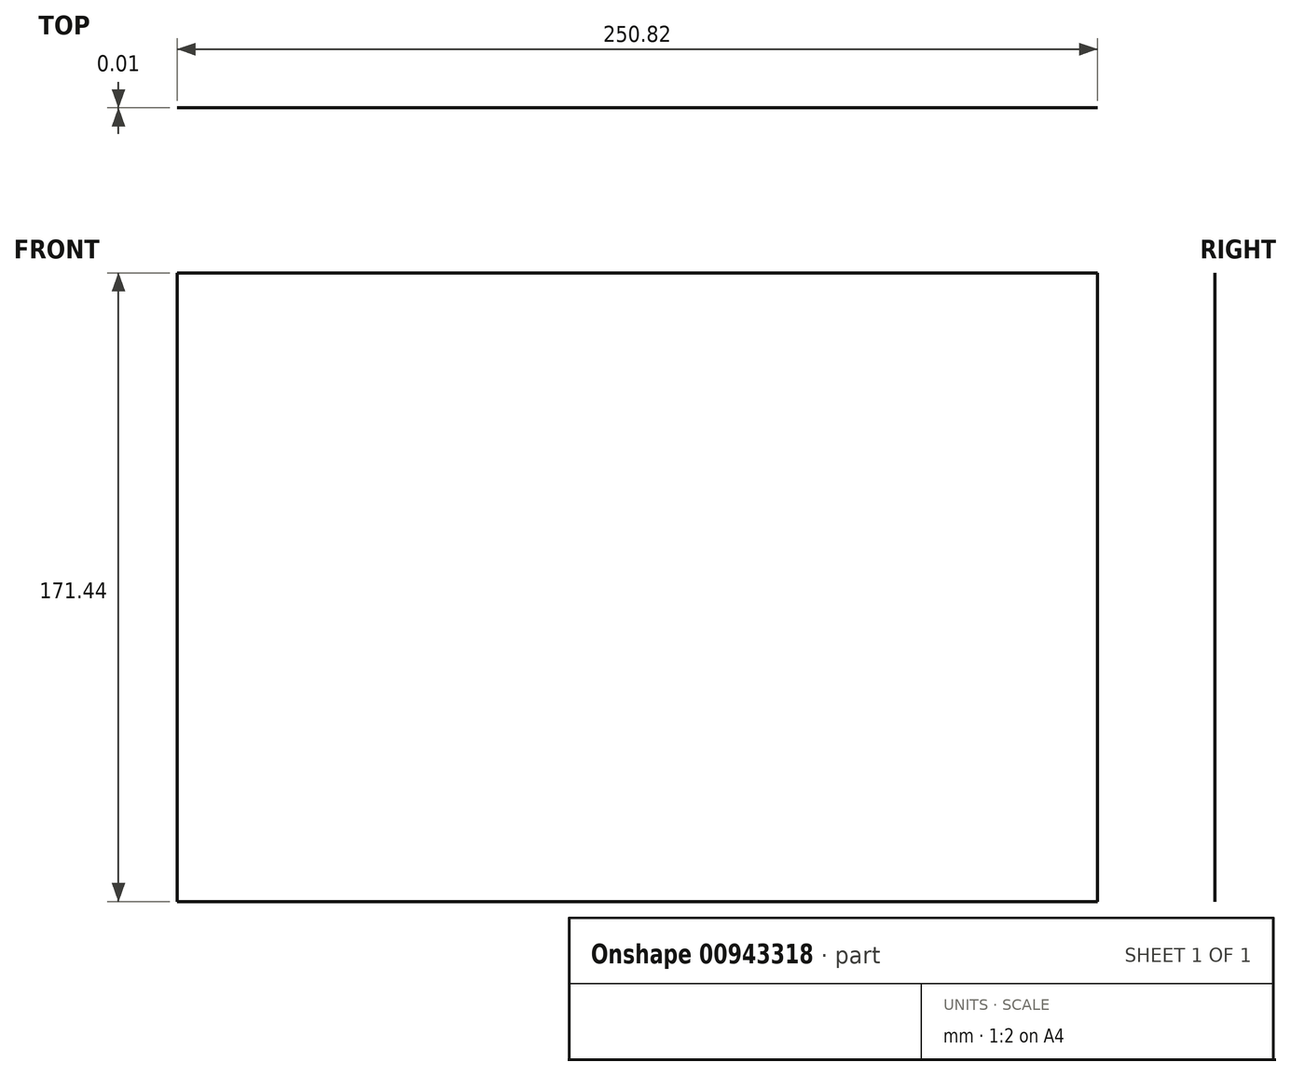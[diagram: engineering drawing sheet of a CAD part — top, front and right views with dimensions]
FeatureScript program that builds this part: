
annotation { "Feature Type Name" : "Feature", "Feature Type Description" : "" }
export const myFeature = defineFeature(function(context is Context, id is Id, definition is map)
    precondition{}
    {
        {
            var Q0;
            Q0=qCreatedBy(makeId("Front.planeOp"),FACE);
            var sketch = newSketch(context, id + "F0", { "sketchPlane" : qUnion([Q0])});
            skLineSegment(sketch, "E0.bottom", {"start": v(125.41, 85.73) * mm, "end": v(-125.41, 85.73) * mm});
            skLineSegment(sketch, "E0.top", {"start": v(125.41, -85.73) * mm, "end": v(-125.41, -85.73) * mm});
            skLineSegment(sketch, "E0.left", {"start": v(125.41, 85.73) * mm, "end": v(125.41, -85.73) * mm});
            skLineSegment(sketch, "E0.right", {"start": v(-125.41, 85.73) * mm, "end": v(-125.41, -85.73) * mm});
            skPoint(sketch, "E0.middle", {"position": v(0, 0) * mm});
            skSolve(sketch);
        }
        {
            var Q0;
            Q0 = qSketchRegion(id + "F0", true);
            extrude(context, id + "F1", {"entities" : qUnion([Q0]), "depth" : 2 / 203.2 * mm, "offsetDistance" : 25.4 * mm});
        }
    });
